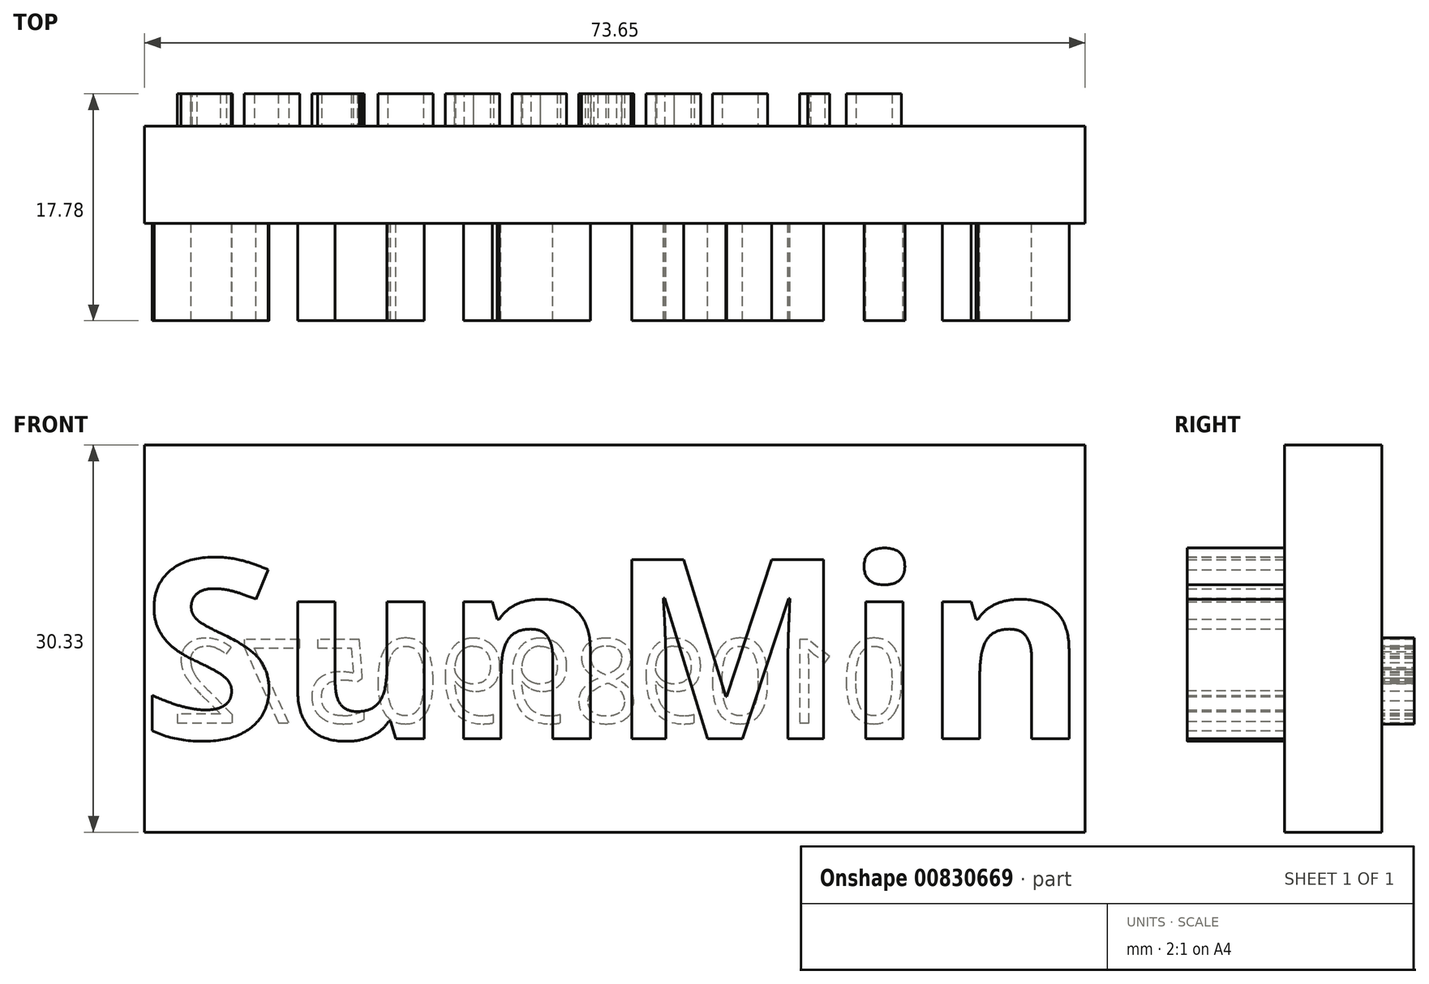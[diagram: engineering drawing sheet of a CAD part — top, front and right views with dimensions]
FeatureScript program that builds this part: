
annotation { "Feature Type Name" : "Feature", "Feature Type Description" : "" }
export const myFeature = defineFeature(function(context is Context, id is Id, definition is map)
    precondition{}
    {
        {
            var Q0;
            Q0=qCreatedBy(makeId("Front.planeOp"),FACE);
            var sketch = newSketch(context, id + "F0", { "sketchPlane" : qUnion([Q0])});
            skLineSegment(sketch, "E0.bottom", {"start": v(0, 0) * mm, "end": v(73.65, 0) * mm});
            skLineSegment(sketch, "E0.top", {"start": v(0, 30.33) * mm, "end": v(73.65, 30.33) * mm});
            skLineSegment(sketch, "E0.left", {"start": v(0, 0) * mm, "end": v(0, 30.33) * mm});
            skLineSegment(sketch, "E0.right", {"start": v(73.65, 0) * mm, "end": v(73.65, 30.33) * mm});
            skSolve(sketch);
        }
        {
            var Q0;
            Q0=makeQuery(id+"F0.imprint","IMPRINT",FACE,{"disambiguationData":[TD([[makeQuery(id+"F0.imprint","IMPRINT",EDGE,{"derivedFrom":sQuery(id+"F0.wireOp",EDGE,"E0.bottom")}),1.0]])]});
            extrude(context, id + "F1", {"entities" : qUnion([Q0]), "depth" : 7.62 * mm, "offsetDistance" : 25.4 * mm});
        }
        {
            var Q0;
            Q0=makeQuery(id+"F1.opExtrude","CAP_FACE",FACE,{"disambiguationData":[OSD([sQuery(id+"F0.wireOp",EDGE,"E0.bottom"),sQuery(id+"F0.wireOp",EDGE,"E0.top"),sQuery(id+"F0.wireOp",EDGE,"E0.left"),sQuery(id+"F0.wireOp",EDGE,"E0.right")])],"isStart":false});
            var sketch = newSketch(context, id + "F2", { "sketchPlane" : qUnion([Q0])});
            skText(sketch, "E1", { "text": "SunMin", "fontName": "OpenSans-Bold.ttf"});
            const initialGuessF2  = {"E1": [-0.00033, 0.00731, 1, 0, 0.01417]};
            skSetInitialGuess(sketch, initialGuessF2);
            skSolve(sketch);
        }
        {
            var Q0;
            Q0=makeQuery(id+"F2.imprint","IMPRINT",FACE,{"disambiguationData":[TD([[makeQuery(id+"F2.imprint","IMPRINT",EDGE,{"derivedFrom":sQuery(id+"F2.wireOp",EDGE,"E1.sketch_text.stroke-28")}),-1.0]])]});
            var Q1;
            Q1 = qSketchRegion(id + "F2", true);
            extrude(context, id + "F3", {"entities" : qUnion([Q0, Q1]), "operationType" : NewBodyOperationType.ADD, "depth" : 7.62 * mm, "offsetDistance" : 25.4 * mm});
        }
        {
            var Q0;
            Q0=makeQuery(id+"F1.opExtrude","CAP_FACE",FACE,{"disambiguationData":[OSD([sQuery(id+"F0.wireOp",EDGE,"E0.bottom"),sQuery(id+"F0.wireOp",EDGE,"E0.top"),sQuery(id+"F0.wireOp",EDGE,"E0.left"),sQuery(id+"F0.wireOp",EDGE,"E0.right")])],"isStart":true});
            var sketch = newSketch(context, id + "F4", { "sketchPlane" : qUnion([Q0])});
            skText(sketch, "E2", { "text": "01098990572", "fontName": "OpenSans-Regular.ttf"});
            skPoint(sketch, "E2.firstSnap0", {"position": v(-73.65, 15.16) * mm});
            const initialGuessF4  = {"E2": [-0.05973, 0.00857, 1, 0, 0.0066]};
            skSetInitialGuess(sketch, initialGuessF4);
            skSolve(sketch);
        }
        {
            var Q0;
            Q0 = qSketchRegion(id + "F4", true);
            extrude(context, id + "F5", {"entities" : qUnion([Q0]), "operationType" : NewBodyOperationType.ADD, "depth" : 2.54 * mm, "offsetDistance" : 25.4 * mm});
        }
    });
